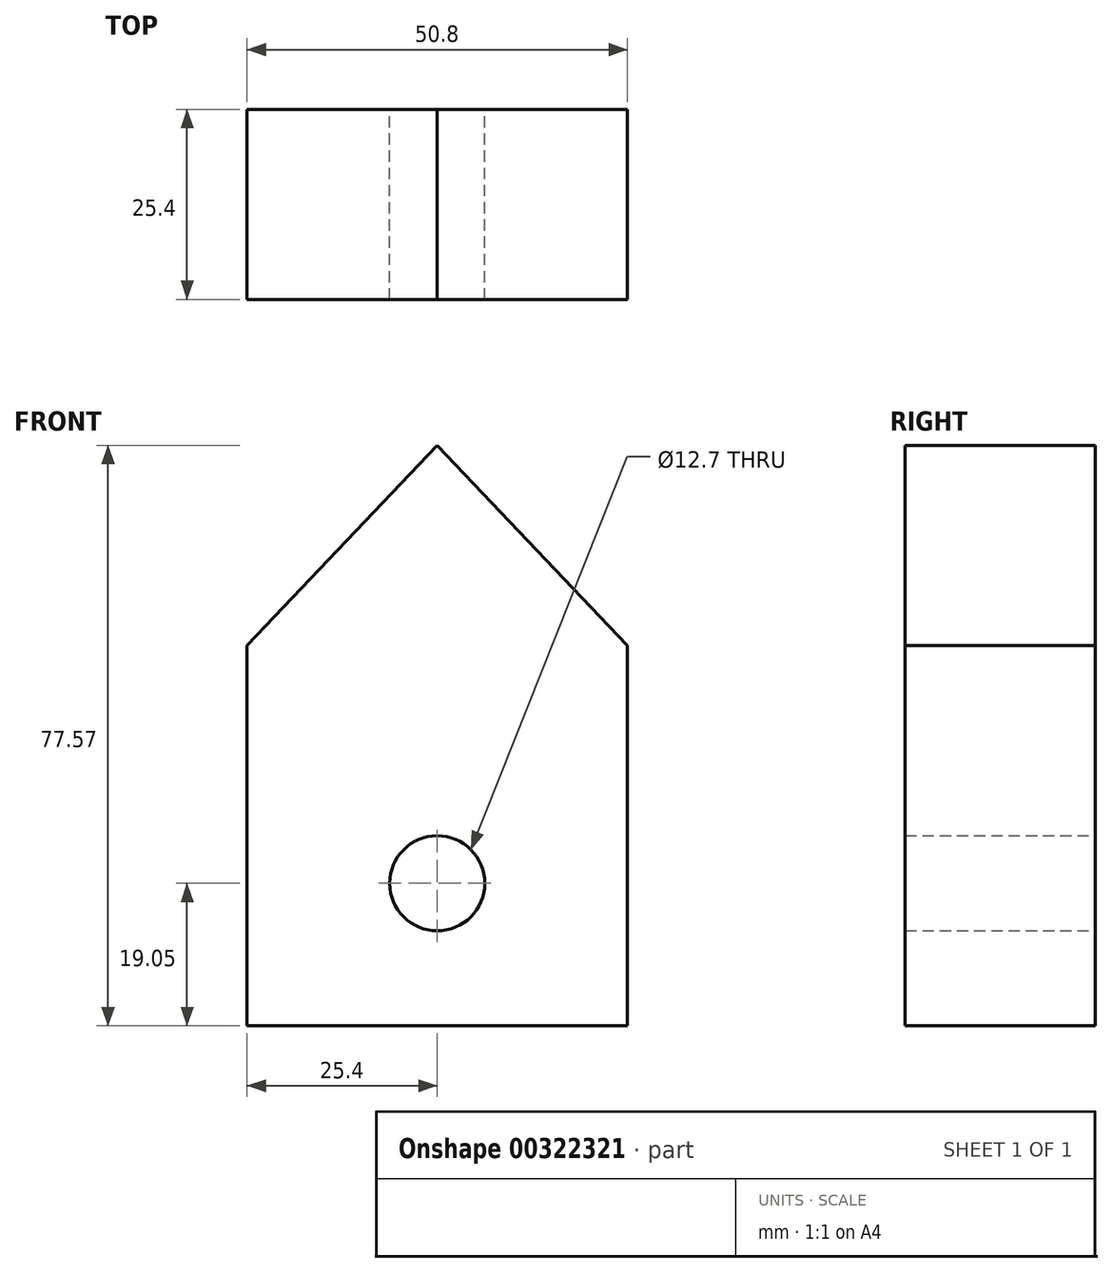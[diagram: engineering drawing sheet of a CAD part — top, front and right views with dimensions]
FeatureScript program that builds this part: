
annotation { "Feature Type Name" : "Feature", "Feature Type Description" : "" }
export const myFeature = defineFeature(function(context is Context, id is Id, definition is map)
    precondition{}
    {
        {
            var Q0;
            Q0=qCreatedBy(makeId("Front.planeOp"),FACE);
            var sketch = newSketch(context, id + "F0", { "sketchPlane" : qUnion([Q0])});
            skLineSegment(sketch, "E0.bottom", {"start": v(25.4, -25.4) * mm, "end": v(-25.4, -25.4) * mm});
            skLineSegment(sketch, "E0.left", {"start": v(25.4, -25.4) * mm, "end": v(25.4, 25.4) * mm});
            skLineSegment(sketch, "E0.right", {"start": v(-25.4, -25.4) * mm, "end": v(-25.4, 25.4) * mm});
            skPoint(sketch, "E0.middle", {"position": v(0, 0) * mm});
            skLineSegment(sketch, "E1", {"start": v(-25.4, 25.4) * mm, "end": v(0, 52.17) * mm});
            skLineSegment(sketch, "E2", {"start": v(25.4, 25.4) * mm, "end": v(0, 52.17) * mm});
            skCircle(sketch, "E3", {"center": v(0, -6.35) * mm, "radius": 6.35 * mm});
            skSolve(sketch);
        }
        {
            var Q0;
            Q0 = qSketchRegion(id + "F0", true);
            extrude(context, id + "F1", {"entities" : qUnion([Q0]), "depth" : 25.4 * mm});
        }
    });
